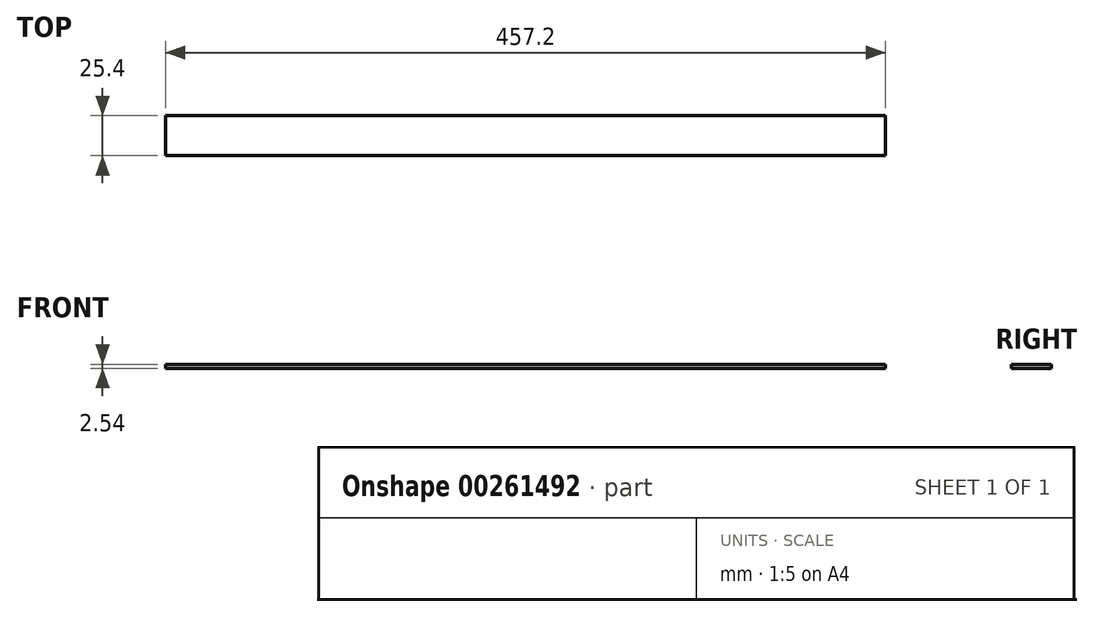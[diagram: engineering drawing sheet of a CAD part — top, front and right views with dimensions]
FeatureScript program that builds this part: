
annotation { "Feature Type Name" : "Feature", "Feature Type Description" : "" }
export const myFeature = defineFeature(function(context is Context, id is Id, definition is map)
    precondition{}
    {
        {
            var Q0;
            Q0=qCreatedBy(makeId("Top.planeOp"),FACE);
            var sketch = newSketch(context, id + "F0", { "sketchPlane" : qUnion([Q0])});
            skLineSegment(sketch, "E0.bottom", {"start": v(-60.75, 1.12) * mm, "end": v(396.45, 1.12) * mm});
            skLineSegment(sketch, "E0.top", {"start": v(-60.75, -24.28) * mm, "end": v(396.45, -24.28) * mm});
            skLineSegment(sketch, "E0.left", {"start": v(-60.75, 1.12) * mm, "end": v(-60.75, -24.28) * mm});
            skLineSegment(sketch, "E0.right", {"start": v(396.45, 1.12) * mm, "end": v(396.45, -24.28) * mm});
            skSolve(sketch);
        }
        {
            var Q0;
            Q0=makeQuery(id+"F0.imprint","IMPRINT",FACE,{"disambiguationData":[TD([[makeQuery(id+"F0.imprint","IMPRINT",EDGE,{"derivedFrom":sQuery(id+"F0.wireOp",EDGE,"E0.bottom")}),-1.0]])]});
            extrude(context, id + "F1", {"entities" : qUnion([Q0]), "depth" : 2.54 * mm});
        }
    });
